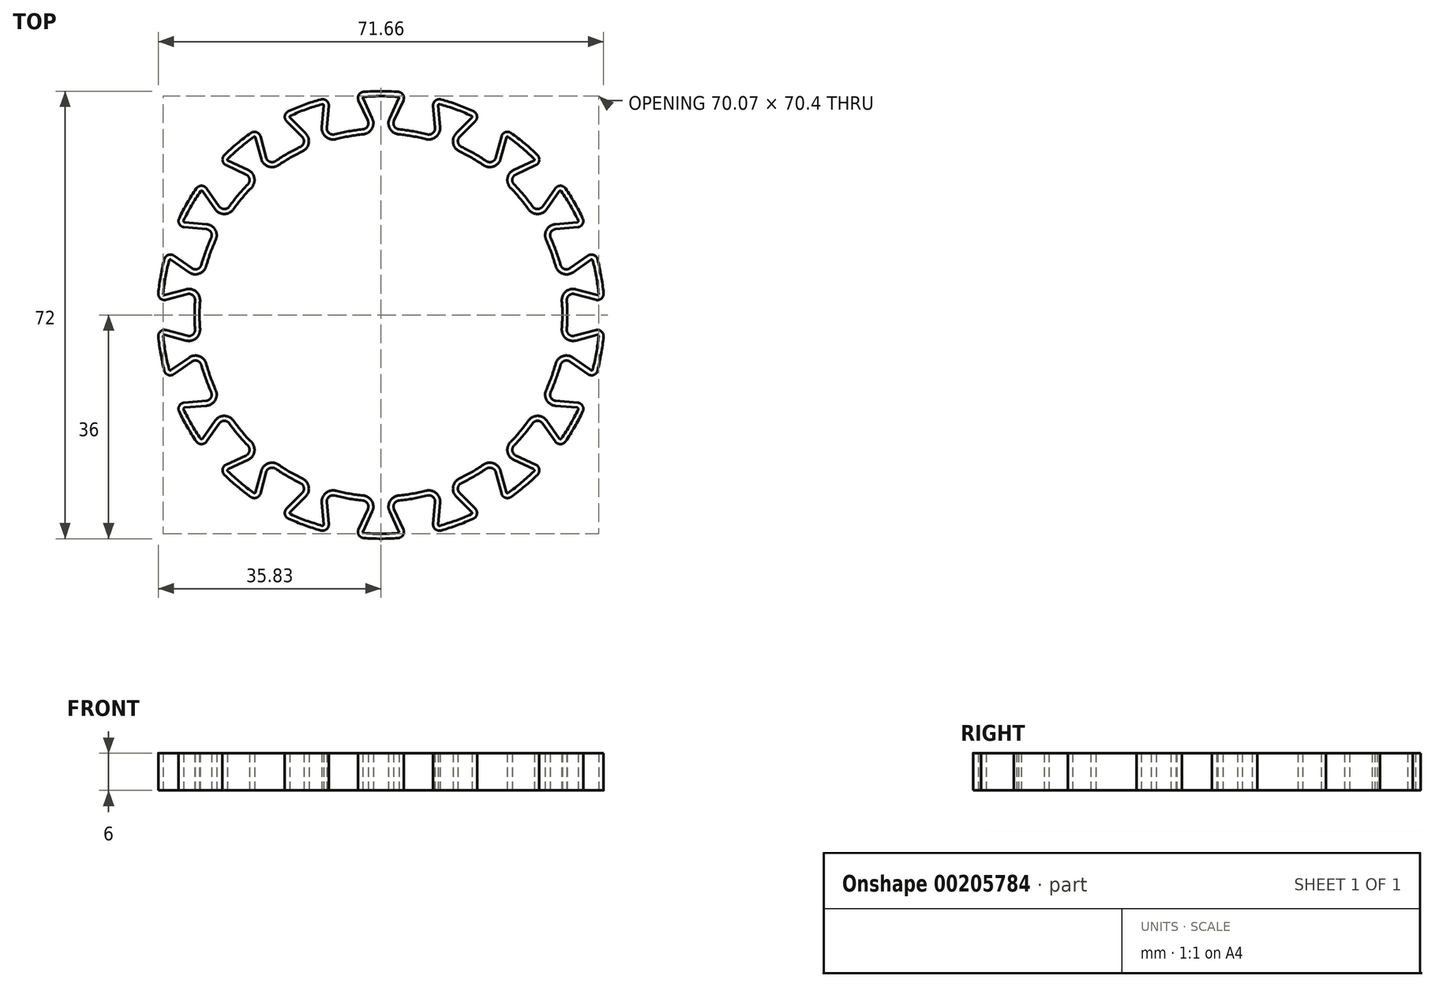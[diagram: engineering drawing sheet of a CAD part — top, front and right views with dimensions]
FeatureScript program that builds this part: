
annotation { "Feature Type Name" : "Feature", "Feature Type Description" : "" }
export const myFeature = defineFeature(function(context is Context, id is Id, definition is map)
    precondition{}
    {
        {
            assignVariable(context, id + "F0", {"name" : "Zigzag", "anyValue" : 18});
        }
        {
            var Q0;
            Q0=qCreatedBy(makeId("Top.planeOp"),FACE);
            var sketch = newSketch(context, id + "F1", { "sketchPlane" : qUnion([Q0])});
            skCircle(sketch, "E0", {"center": v(0, 0) * mm, "radius": 30 * mm});
            skSolve(sketch);
        }
        {
            var Q0;
            Q0=qCreatedBy(makeId("Top.planeOp"),FACE);
            var sketch = newSketch(context, id + "F2", { "sketchPlane" : qUnion([Q0])});
            skCircle(sketch, "E1.0", {"center": v(0, 0) * mm, "radius": 30 * mm});
            skCircle(sketch, "E2.0", {"center": v(0, 0) * mm, "radius": 36 * mm});
            skSolve(sketch);
        }
        {
            var Q0;
            Q0=qCreatedBy(makeId("Top.planeOp"),FACE);
            var sketch = newSketch(context, id + "F3", { "sketchPlane" : qUnion([Q0])});
            skLineSegment(sketch, "E3", {"start": v(0, 0) * mm, "end": v(0, 36) * mm, "construction": true});
            skLineSegment(sketch, "E4", {"start": v(0, 36) * mm, "end": v(0, 30) * mm});
            skPoint(sketch, "E5", {"position": v(0, 33) * mm});
            skCircle(sketch, "E6.0", {"center": v(0, 0) * mm, "radius": 36 * mm});
            skCircle(sketch, "E7.0", {"center": v(0, 0) * mm, "radius": 30 * mm});
            skLineSegment(sketch, "E8", {"start": v(4.2, 35.75) * mm, "end": v(1.5, 29.96) * mm});
            skLineSegment(sketch, "E9.MirrorCS", {"start": v(-4.2, 35.75) * mm, "end": v(-1.5, 29.96) * mm});
            skPoint(sketch, "E10", {"position": v(-2.85, 32.86) * mm});
            skPoint(sketch, "E11", {"position": v(2.85, 32.86) * mm});
            skArc(sketch, "E12", {"start": v(2.85, 32.86) * mm, "mid": v(0, 33) * mm, "end": v(-2.85, 32.86) * mm, "construction": true});
            skSolve(sketch);
        }
        {
            var Q0;
            Q0=qCreatedBy(makeId("Top.planeOp"),FACE);
            var sketch = newSketch(context, id + "F4", { "sketchPlane" : qUnion([Q0])});
            skLineSegment(sketch, "E13.0", {"start": v(-3.6, 34.47) * mm, "end": v(-2.11, 31.28) * mm});
            skLineSegment(sketch, "E13.1", {"start": v(3.6, 34.47) * mm, "end": v(2.11, 31.28) * mm});
            skArc(sketch, "E14", {"start": v(2.77, 35.9) * mm, "mid": v(0, 36) * mm, "end": v(-2.77, 35.9) * mm});
            skArc(sketch, "E15", {"start": v(5.2, 29.54) * mm, "mid": v(4.07, 29.72) * mm, "end": v(2.92, 29.86) * mm});
            skPoint(sketch, "E16.center", {"position": v(-1.5, 29.96) * mm});
            skPoint(sketch, "E17.visualSharp", {"position": v(-4.2, 35.75) * mm});
            skArc(sketch, "E17.filletArc", {"start": v(-2.77, 35.9) * mm, "mid": v(-3.56, 35.4) * mm, "end": v(-3.6, 34.47) * mm});
            skPoint(sketch, "E18.visualSharp", {"position": v(4.2, 35.75) * mm});
            skArc(sketch, "E18.filletArc", {"start": v(3.6, 34.47) * mm, "mid": v(3.56, 35.4) * mm, "end": v(2.77, 35.9) * mm});
            skPoint(sketch, "E19.visualSharp", {"position": v(1.5, 29.96) * mm});
            skArc(sketch, "E19.filletArc", {"start": v(2.11, 31.28) * mm, "mid": v(2.15, 30.36) * mm, "end": v(2.92, 29.86) * mm});
            skArc(sketch, "E20.filletArc", {"start": v(-2.92, 29.86) * mm, "mid": v(-2.15, 30.36) * mm, "end": v(-2.11, 31.28) * mm});
            skLineSegment(sketch, "E21", {"start": v(-5.2, 29.54) * mm, "end": v(0, 0) * mm, "construction": true});
            skLineSegment(sketch, "E22", {"start": v(0, 0) * mm, "end": v(5.2, 29.54) * mm, "construction": true});
            skLineSegment(sketch, "E23", {"start": v(0, 36) * mm, "end": v(0, 0) * mm, "construction": true});
            skArc(sketch, "E24.MirrorCS", {"start": v(-5.2, 29.54) * mm, "mid": v(-4.07, 29.72) * mm, "end": v(-2.92, 29.86) * mm});
            skSolve(sketch);
        }
        {
            var Q0;
            Q0=qCreatedBy(makeId("Top.planeOp"),FACE);
            var sketch = newSketch(context, id + "F5", { "sketchPlane" : qUnion([Q0])});
            skArc(sketch, "E25.0", {"start": v(5.2, 29.54) * mm, "mid": v(4.07, 29.72) * mm, "end": v(2.92, 29.86) * mm});
            skArc(sketch, "E25.1", {"start": v(2.77, 35.9) * mm, "mid": v(0, 36) * mm, "end": v(-2.77, 35.9) * mm});
            skArc(sketch, "E25.2", {"start": v(-5.2, 29.54) * mm, "mid": v(-4.07, 29.72) * mm, "end": v(-2.92, 29.86) * mm});
            skArc(sketch, "E25.3", {"start": v(-2.92, 29.86) * mm, "mid": v(-2.15, 30.36) * mm, "end": v(-2.11, 31.28) * mm});
            skLineSegment(sketch, "E25.4", {"start": v(3.6, 34.47) * mm, "end": v(2.11, 31.28) * mm});
            skArc(sketch, "E25.5", {"start": v(3.6, 34.47) * mm, "mid": v(3.56, 35.4) * mm, "end": v(2.77, 35.9) * mm});
            skArc(sketch, "E25.6", {"start": v(2.11, 31.28) * mm, "mid": v(2.15, 30.36) * mm, "end": v(2.92, 29.86) * mm});
            skLineSegment(sketch, "E25.7", {"start": v(-3.6, 34.47) * mm, "end": v(-2.11, 31.28) * mm});
            skArc(sketch, "E25.8", {"start": v(-2.77, 35.9) * mm, "mid": v(-3.56, 35.4) * mm, "end": v(-3.6, 34.47) * mm});
            skLineSegment(sketch, "E26.0", {"start": v(-5.2, 29.54) * mm, "end": v(0, 0) * mm});
            skLineSegment(sketch, "E26.1", {"start": v(0, 0) * mm, "end": v(5.2, 29.54) * mm});
            skSolve(sketch);
        }
        {
            var Q0;
            Q0 = qSketchRegion(id + "F5", true);
            extrude(context, id + "F6", {"entities" : qUnion([Q0]), "depth" : 6 * mm});
        }
        {
            var Q0;
            Q0=makeQuery(id+"F6.opExtrude","SWEPT_BODY",BODY,{"disambiguationData":[OSD([sQuery(id+"F5.wireOp",EDGE,"E25.0"),sQuery(id+"F5.wireOp",EDGE,"E25.1"),sQuery(id+"F5.wireOp",EDGE,"E25.2"),sQuery(id+"F5.wireOp",EDGE,"E25.3"),sQuery(id+"F5.wireOp",EDGE,"E25.4"),sQuery(id+"F5.wireOp",EDGE,"E25.5"),sQuery(id+"F5.wireOp",EDGE,"E25.6"),sQuery(id+"F5.wireOp",EDGE,"E25.7"),sQuery(id+"F5.wireOp",EDGE,"E25.8"),sQuery(id+"F5.wireOp",EDGE,"E26.0"),sQuery(id+"F5.wireOp",EDGE,"E26.1")])]});
            var Q1;
            Q1=makeQuery(id+"F6.opExtrude","SWEPT_EDGE",EDGE,{"disambiguationData":[OSD([sQuery(id+"F5.wireOp",EDGE,"E26.0"),sQuery(id+"F5.wireOp",EDGE,"E26.1")])]});
            circularPattern(context, id + "F7", {"operationType" : NewBodyOperationType.ADD, "entities" : qUnion([Q0]), "axis" : qUnion([Q1]), "angle" : 360 * degree, "instanceCount" : getVariable(context, 'Zigzag'), "oppositeDirection" : true, "equalSpace" : true, "computeTransformsWithoutBuiltin" : true});
        }
        {
            var Q0;
            {var subQ0=makeQuery(id+"F6.opExtrude","CAP_FACE",FACE,{"disambiguationData":[OSD([sQuery(id+"F5.wireOp",EDGE,"E25.0"),sQuery(id+"F5.wireOp",EDGE,"E25.1"),sQuery(id+"F5.wireOp",EDGE,"E25.2"),sQuery(id+"F5.wireOp",EDGE,"E25.3"),sQuery(id+"F5.wireOp",EDGE,"E25.4"),sQuery(id+"F5.wireOp",EDGE,"E25.5"),sQuery(id+"F5.wireOp",EDGE,"E25.6"),sQuery(id+"F5.wireOp",EDGE,"E25.7"),sQuery(id+"F5.wireOp",EDGE,"E25.8"),sQuery(id+"F5.wireOp",EDGE,"E26.0"),sQuery(id+"F5.wireOp",EDGE,"E26.1")])],"isStart":false});Q0=makeQuery(id+"F7.boolean.opBoolean","MERGE",FACE,{"derivedFrom":[subQ0,makeQuery(id+"F7.opPattern","COPY",FACE,{"derivedFrom":subQ0,"instanceName":"1"}),makeQuery(id+"F7.opPattern","COPY",FACE,{"derivedFrom":subQ0,"instanceName":"2"}),makeQuery(id+"F7.opPattern","COPY",FACE,{"derivedFrom":subQ0,"instanceName":"3"}),makeQuery(id+"F7.opPattern","COPY",FACE,{"derivedFrom":subQ0,"instanceName":"4"}),makeQuery(id+"F7.opPattern","COPY",FACE,{"derivedFrom":subQ0,"instanceName":"5"}),makeQuery(id+"F7.opPattern","COPY",FACE,{"derivedFrom":subQ0,"instanceName":"6"}),makeQuery(id+"F7.opPattern","COPY",FACE,{"derivedFrom":subQ0,"instanceName":"7"}),makeQuery(id+"F7.opPattern","COPY",FACE,{"derivedFrom":subQ0,"instanceName":"8"}),makeQuery(id+"F7.opPattern","COPY",FACE,{"derivedFrom":subQ0,"instanceName":"9"}),makeQuery(id+"F7.opPattern","COPY",FACE,{"derivedFrom":subQ0,"instanceName":"10"}),makeQuery(id+"F7.opPattern","COPY",FACE,{"derivedFrom":subQ0,"instanceName":"11"}),makeQuery(id+"F7.opPattern","COPY",FACE,{"derivedFrom":subQ0,"instanceName":"12"}),makeQuery(id+"F7.opPattern","COPY",FACE,{"derivedFrom":subQ0,"instanceName":"13"}),makeQuery(id+"F7.opPattern","COPY",FACE,{"derivedFrom":subQ0,"instanceName":"14"}),makeQuery(id+"F7.opPattern","COPY",FACE,{"derivedFrom":subQ0,"instanceName":"15"}),makeQuery(id+"F7.opPattern","COPY",FACE,{"derivedFrom":subQ0,"instanceName":"16"}),makeQuery(id+"F7.opPattern","COPY",FACE,{"derivedFrom":subQ0,"instanceName":"17"})]});}
            var Q1;
            {var subQ0=makeQuery(id+"F6.opExtrude","CAP_FACE",FACE,{"disambiguationData":[OSD([sQuery(id+"F5.wireOp",EDGE,"E25.0"),sQuery(id+"F5.wireOp",EDGE,"E25.1"),sQuery(id+"F5.wireOp",EDGE,"E25.2"),sQuery(id+"F5.wireOp",EDGE,"E25.3"),sQuery(id+"F5.wireOp",EDGE,"E25.4"),sQuery(id+"F5.wireOp",EDGE,"E25.5"),sQuery(id+"F5.wireOp",EDGE,"E25.6"),sQuery(id+"F5.wireOp",EDGE,"E25.7"),sQuery(id+"F5.wireOp",EDGE,"E25.8"),sQuery(id+"F5.wireOp",EDGE,"E26.0"),sQuery(id+"F5.wireOp",EDGE,"E26.1")])],"isStart":true});Q1=makeQuery(id+"F7.boolean.opBoolean","MERGE",FACE,{"derivedFrom":[subQ0,makeQuery(id+"F7.opPattern","COPY",FACE,{"derivedFrom":subQ0,"instanceName":"1"}),makeQuery(id+"F7.opPattern","COPY",FACE,{"derivedFrom":subQ0,"instanceName":"2"}),makeQuery(id+"F7.opPattern","COPY",FACE,{"derivedFrom":subQ0,"instanceName":"3"}),makeQuery(id+"F7.opPattern","COPY",FACE,{"derivedFrom":subQ0,"instanceName":"4"}),makeQuery(id+"F7.opPattern","COPY",FACE,{"derivedFrom":subQ0,"instanceName":"5"}),makeQuery(id+"F7.opPattern","COPY",FACE,{"derivedFrom":subQ0,"instanceName":"6"}),makeQuery(id+"F7.opPattern","COPY",FACE,{"derivedFrom":subQ0,"instanceName":"7"}),makeQuery(id+"F7.opPattern","COPY",FACE,{"derivedFrom":subQ0,"instanceName":"8"}),makeQuery(id+"F7.opPattern","COPY",FACE,{"derivedFrom":subQ0,"instanceName":"9"}),makeQuery(id+"F7.opPattern","COPY",FACE,{"derivedFrom":subQ0,"instanceName":"10"}),makeQuery(id+"F7.opPattern","COPY",FACE,{"derivedFrom":subQ0,"instanceName":"11"}),makeQuery(id+"F7.opPattern","COPY",FACE,{"derivedFrom":subQ0,"instanceName":"12"}),makeQuery(id+"F7.opPattern","COPY",FACE,{"derivedFrom":subQ0,"instanceName":"13"}),makeQuery(id+"F7.opPattern","COPY",FACE,{"derivedFrom":subQ0,"instanceName":"14"}),makeQuery(id+"F7.opPattern","COPY",FACE,{"derivedFrom":subQ0,"instanceName":"15"}),makeQuery(id+"F7.opPattern","COPY",FACE,{"derivedFrom":subQ0,"instanceName":"16"}),makeQuery(id+"F7.opPattern","COPY",FACE,{"derivedFrom":subQ0,"instanceName":"17"})]});}
            var Q2;
            Q2=makeQuery(id+"FKFrLr9VvKz1Pv2_1.opExtrude","SWEPT_BODY",BODY,{"disambiguationData":[OSD([sQuery(id+"F4.wireOp",EDGE,"E13.0"),sQuery(id+"F4.wireOp",EDGE,"E13.1"),sQuery(id+"F4.wireOp",EDGE,"E14"),sQuery(id+"F4.wireOp",EDGE,"E15"),sQuery(id+"F4.wireOp",EDGE,"E16.1.0"),sQuery(id+"F4.wireOp",EDGE,"E16.1.1"),sQuery(id+"F4.wireOp",EDGE,"E16.1.2"),sQuery(id+"F4.wireOp",EDGE,"E16.1.3"),sQuery(id+"F4.wireOp",EDGE,"E16.2.0"),sQuery(id+"F4.wireOp",EDGE,"E16.2.1"),sQuery(id+"F4.wireOp",EDGE,"E16.2.2"),sQuery(id+"F4.wireOp",EDGE,"E16.2.3"),sQuery(id+"F4.wireOp",EDGE,"E16.3.0"),sQuery(id+"F4.wireOp",EDGE,"E16.3.1"),sQuery(id+"F4.wireOp",EDGE,"E16.3.2"),sQuery(id+"F4.wireOp",EDGE,"E16.3.3"),sQuery(id+"F4.wireOp",EDGE,"E16.4.0"),sQuery(id+"F4.wireOp",EDGE,"E16.4.1"),sQuery(id+"F4.wireOp",EDGE,"E16.4.2"),sQuery(id+"F4.wireOp",EDGE,"E16.4.3"),sQuery(id+"F4.wireOp",EDGE,"E16.5.0"),sQuery(id+"F4.wireOp",EDGE,"E16.5.1"),sQuery(id+"F4.wireOp",EDGE,"E16.5.2"),sQuery(id+"F4.wireOp",EDGE,"E16.5.3"),sQuery(id+"F4.wireOp",EDGE,"E16.6.0"),sQuery(id+"F4.wireOp",EDGE,"E16.6.1"),sQuery(id+"F4.wireOp",EDGE,"E16.6.2"),sQuery(id+"F4.wireOp",EDGE,"E16.6.3"),sQuery(id+"F4.wireOp",EDGE,"E16.7.0"),sQuery(id+"F4.wireOp",EDGE,"E16.7.1"),sQuery(id+"F4.wireOp",EDGE,"E16.7.2"),sQuery(id+"F4.wireOp",EDGE,"E16.7.3"),sQuery(id+"F4.wireOp",EDGE,"E16.8.0"),sQuery(id+"F4.wireOp",EDGE,"E16.8.1"),sQuery(id+"F4.wireOp",EDGE,"E16.8.2"),sQuery(id+"F4.wireOp",EDGE,"E16.8.3"),sQuery(id+"F4.wireOp",EDGE,"E16.9.0"),sQuery(id+"F4.wireOp",EDGE,"E16.9.1"),sQuery(id+"F4.wireOp",EDGE,"E16.9.2"),sQuery(id+"F4.wireOp",EDGE,"E16.9.3"),sQuery(id+"F4.wireOp",EDGE,"E16.10.0"),sQuery(id+"F4.wireOp",EDGE,"E16.10.1"),sQuery(id+"F4.wireOp",EDGE,"E16.10.2"),sQuery(id+"F4.wireOp",EDGE,"E16.10.3"),sQuery(id+"F4.wireOp",EDGE,"E16.11.0"),sQuery(id+"F4.wireOp",EDGE,"E16.11.1"),sQuery(id+"F4.wireOp",EDGE,"E16.11.2"),sQuery(id+"F4.wireOp",EDGE,"E16.11.3"),sQuery(id+"F4.wireOp",EDGE,"E16.12.0"),sQuery(id+"F4.wireOp",EDGE,"E16.12.1"),sQuery(id+"F4.wireOp",EDGE,"E16.12.2"),sQuery(id+"F4.wireOp",EDGE,"E16.12.3"),sQuery(id+"F4.wireOp",EDGE,"E16.13.0"),sQuery(id+"F4.wireOp",EDGE,"E16.13.1"),sQuery(id+"F4.wireOp",EDGE,"E16.13.2"),sQuery(id+"F4.wireOp",EDGE,"E16.13.3"),sQuery(id+"F4.wireOp",EDGE,"E16.14.0"),sQuery(id+"F4.wireOp",EDGE,"E16.14.1"),sQuery(id+"F4.wireOp",EDGE,"E16.14.2"),sQuery(id+"F4.wireOp",EDGE,"E16.14.3"),sQuery(id+"F4.wireOp",EDGE,"E16.15.0"),sQuery(id+"F4.wireOp",EDGE,"E16.15.1"),sQuery(id+"F4.wireOp",EDGE,"E16.15.2"),sQuery(id+"F4.wireOp",EDGE,"E16.15.3"),sQuery(id+"F4.wireOp",EDGE,"d89f925d-01bf-4e6b-843d-d6b501c543c5.3.16.0"),sQuery(id+"F4.wireOp",EDGE,"d89f925d-01bf-4e6b-843d-d6b501c543c5.4.16.0"),sQuery(id+"F4.wireOp",EDGE,"d89f925d-01bf-4e6b-843d-d6b501c543c5.8.16.0"),sQuery(id+"F4.wireOp",EDGE,"d89f925d-01bf-4e6b-843d-d6b501c543c5.11.16.0"),sQuery(id+"F4.wireOp",EDGE,"d89f925d-01bf-4e6b-843d-d6b501c543c5.3.17.0"),sQuery(id+"F4.wireOp",EDGE,"d89f925d-01bf-4e6b-843d-d6b501c543c5.4.17.0"),sQuery(id+"F4.wireOp",EDGE,"d89f925d-01bf-4e6b-843d-d6b501c543c5.8.17.0"),sQuery(id+"F4.wireOp",EDGE,"d89f925d-01bf-4e6b-843d-d6b501c543c5.11.17.0")])]});
            shell(context, id + "F8", {"entities" : qUnion([Q0, Q1]), "parts" : qUnion([Q2]), "thickness" : .8 * mm});
        }
    });
